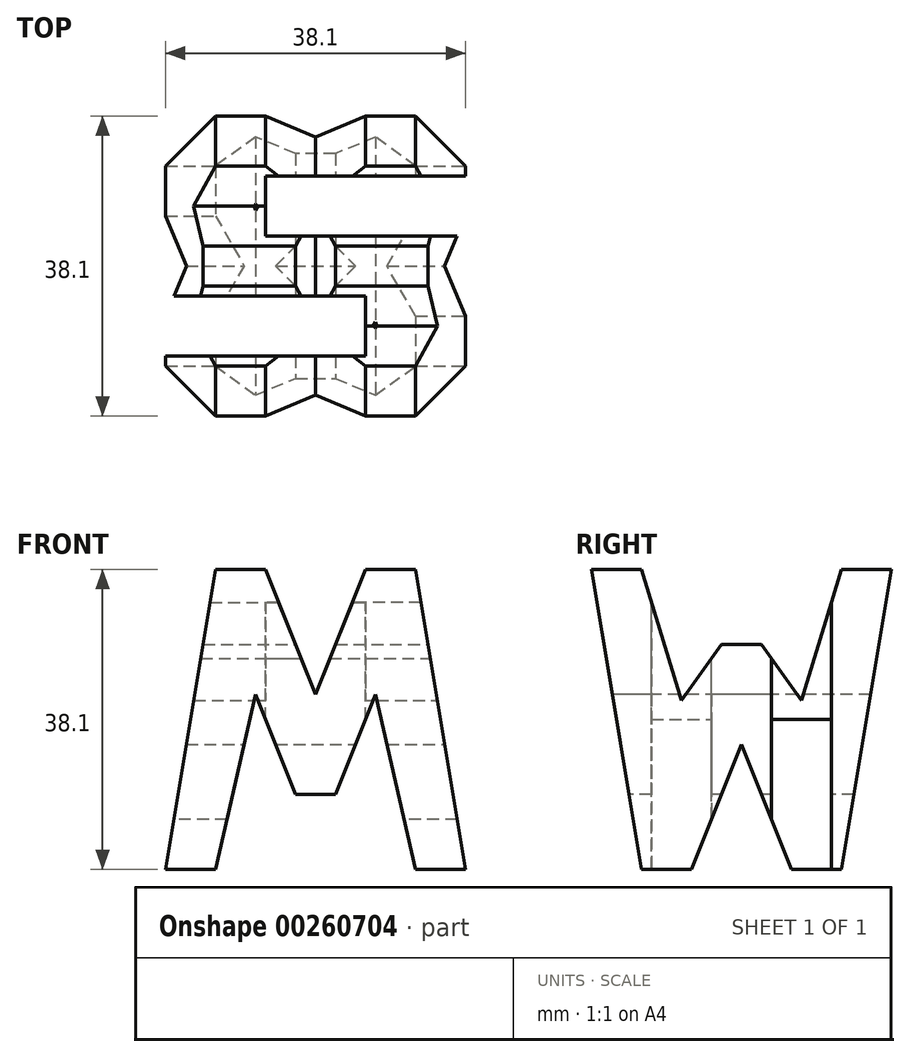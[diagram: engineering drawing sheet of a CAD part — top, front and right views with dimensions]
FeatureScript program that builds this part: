
annotation { "Feature Type Name" : "Feature", "Feature Type Description" : "" }
export const myFeature = defineFeature(function(context is Context, id is Id, definition is map)
    precondition{}
    {
        {
            var Q0;
            Q0=qCreatedBy(makeId("Front.planeOp"),FACE);
            var sketch = newSketch(context, id + "F0", { "sketchPlane" : qUnion([Q0])});
            skLineSegment(sketch, "E0", {"start": v(0, 0) * mm, "end": v(0, 38.1) * mm});
            skLineSegment(sketch, "E1", {"start": v(0, 0) * mm, "end": v(38.1, 0) * mm});
            skLineSegment(sketch, "E2", {"start": v(38.1, 38.1) * mm, "end": v(38.1, 0) * mm});
            skLineSegment(sketch, "E3", {"start": v(38.1, 38.1) * mm, "end": v(0, 38.1) * mm});
            skSolve(sketch);
        }
        {
            var Q0;
            Q0 = qSketchRegion(id + "F0", true);
            extrude(context, id + "F1", {"entities" : qUnion([Q0]), "depth" : 38.1 * mm});
        }
        {
            var Q0;
            Q0=qCreatedBy(makeId("Front.planeOp"),FACE);
            cPlane(context, id + "F2", {"entities" : qUnion([Q0]), "cplaneType" : CPlaneType.OFFSET, "offset" : 38.1 * mm, "width" : 152.4 * mm, "height" : 152.4 * mm});
        }
        {
            var Q0;
            Q0=qCreatedBy(makeId("Right.planeOp"),FACE);
            cPlane(context, id + "F3", {"entities" : qUnion([Q0]), "cplaneType" : CPlaneType.OFFSET, "offset" : 38.1 * mm, "width" : 152.4 * mm, "height" : 152.4 * mm});
        }
        {
            var Q0;
            Q0=qCreatedBy(makeId("Top.planeOp"),FACE);
            cPlane(context, id + "F4", {"entities" : qUnion([Q0]), "cplaneType" : CPlaneType.OFFSET, "offset" : 38.1 * mm, "width" : 152.4 * mm, "height" : 152.4 * mm});
        }
        {
            var Q0;
            Q0=qCreatedBy(id+"F3.planeOp",FACE);
            var sketch = newSketch(context, id + "F5", { "sketchPlane" : qUnion([Q0])});
            skLineSegment(sketch, "E4", {"start": v(0, 0) * mm, "end": v(0, 38.1) * mm});
            skLineSegment(sketch, "E5", {"start": v(0, 38.1) * mm, "end": v(-38.1, 38.1) * mm});
            skLineSegment(sketch, "E6", {"start": v(-38.1, 38.1) * mm, "end": v(-38.1, 0) * mm});
            skLineSegment(sketch, "E7", {"start": v(-38.1, 0) * mm, "end": v(0, 0) * mm});
            skLineSegment(sketch, "E8", {"start": v(-6.35, 0) * mm, "end": v(0, 38.1) * mm});
            skLineSegment(sketch, "E9", {"start": v(-6.35, 38.1) * mm, "end": v(-11.43, 21.48) * mm});
            skLineSegment(sketch, "E10", {"start": v(-11.43, 21.48) * mm, "end": v(-16.51, 28.58) * mm});
            skLineSegment(sketch, "E11", {"start": v(-16.51, 28.58) * mm, "end": v(-21.6, 28.58) * mm});
            skLineSegment(sketch, "E12", {"start": v(-21.6, 28.57) * mm, "end": v(-26.67, 21.48) * mm});
            skPoint(sketch, "E13.end.orphan", {"position": v(-31.75, 38.1) * mm});
            skLineSegment(sketch, "E14", {"start": v(-31.75, 38.1) * mm, "end": v(-26.67, 21.48) * mm});
            skLineSegment(sketch, "E15", {"start": v(-38.1, 38.1) * mm, "end": v(-31.75, 38.1) * mm});
            skLineSegment(sketch, "E16", {"start": v(-38.1, 38.1) * mm, "end": v(-31.75, 0) * mm});
            skLineSegment(sketch, "E17", {"start": v(-31.75, 0) * mm, "end": v(-25.4, 0) * mm});
            skLineSegment(sketch, "E18", {"start": v(-25.4, 0) * mm, "end": v(-19.05, 15.88) * mm});
            skLineSegment(sketch, "E19", {"start": v(-19.05, 15.88) * mm, "end": v(-12.7, 0) * mm});
            skLineSegment(sketch, "E20", {"start": v(-12.7, 0) * mm, "end": v(-6.35, 0) * mm});
            skSolve(sketch);
        }
        {
            var Q0;
            {var subQ2=sQuery(id+"F5.wireOp",EDGE,"E9");Q0=makeQuery(id+"F5.imprint","IMPRINT",FACE,{"disambiguationData":[TD([[makeQuery(id+"F5.imprint","IMPRINT",EDGE,{"derivedFrom":subQ2}),-1.0]])]});}
            var Q1;
            {var subQ0=sQuery(id+"F5.wireOp",EDGE,"E6");Q1=makeQuery(id+"F5.imprint","IMPRINT",FACE,{"disambiguationData":[TD([[makeQuery(id+"F5.imprint","IMPRINT",EDGE,{"derivedFrom":subQ0}),1.0]])]});}
            var Q2;
            {var subQ0=sQuery(id+"F5.wireOp",EDGE,"E18");Q2=makeQuery(id+"F5.imprint","IMPRINT",FACE,{"disambiguationData":[TD([[makeQuery(id+"F5.imprint","IMPRINT",EDGE,{"derivedFrom":subQ0}),-1.0]])]});}
            var Q3;
            {var subQ0=sQuery(id+"F5.wireOp",EDGE,"E4");Q3=makeQuery(id+"F5.imprint","IMPRINT",FACE,{"disambiguationData":[TD([[makeQuery(id+"F5.imprint","IMPRINT",EDGE,{"derivedFrom":subQ0}),1.0]])]});}
            extrude(context, id + "F6", {"entities" : qUnion([Q0, Q1, Q2, Q3]), "operationType" : NewBodyOperationType.REMOVE, "oppositeDirection" : true, "depth" : 38.1 * mm});
        }
        {
            var Q0;
            Q0=qCreatedBy(id+"F2.planeOp",FACE);
            var sketch = newSketch(context, id + "F7", { "sketchPlane" : qUnion([Q0])});
            skLineSegment(sketch, "E21", {"start": v(6.35, 38.1) * mm, "end": v(0, 0) * mm});
            skLineSegment(sketch, "E22", {"start": v(0, 0) * mm, "end": v(6.35, 0) * mm});
            skLineSegment(sketch, "E23", {"start": v(6.35, 0) * mm, "end": v(11.43, 22.22) * mm});
            skLineSegment(sketch, "E24", {"start": v(11.43, 22.22) * mm, "end": v(16.51, 9.52) * mm});
            skLineSegment(sketch, "E25", {"start": v(16.51, 9.52) * mm, "end": v(21.6, 9.52) * mm});
            skLineSegment(sketch, "E26", {"start": v(21.6, 9.52) * mm, "end": v(26.67, 22.22) * mm});
            skLineSegment(sketch, "E27", {"start": v(26.67, 22.22) * mm, "end": v(31.75, 0) * mm});
            skLineSegment(sketch, "E28", {"start": v(31.75, 0) * mm, "end": v(38.1, 0) * mm});
            skLineSegment(sketch, "E29", {"start": v(38.1, 0) * mm, "end": v(31.75, 38.1) * mm});
            skLineSegment(sketch, "E30", {"start": v(31.75, 38.1) * mm, "end": v(25.4, 38.1) * mm});
            skLineSegment(sketch, "E31", {"start": v(25.4, 38.1) * mm, "end": v(19.05, 22.22) * mm});
            skLineSegment(sketch, "E32", {"start": v(19.05, 22.22) * mm, "end": v(12.7, 38.1) * mm});
            skLineSegment(sketch, "E33", {"start": v(12.7, 38.1) * mm, "end": v(6.35, 38.1) * mm});
            skLineSegment(sketch, "E34.bottom", {"start": v(0, 0) * mm, "end": v(38.1, 0) * mm});
            skLineSegment(sketch, "E34.top", {"start": v(0, 38.1) * mm, "end": v(38.1, 38.1) * mm});
            skLineSegment(sketch, "E34.left", {"start": v(0, 0) * mm, "end": v(0, 38.1) * mm});
            skLineSegment(sketch, "E34.right", {"start": v(38.1, 0) * mm, "end": v(38.1, 38.1) * mm});
            skSolve(sketch);
        }
        {
            var Q0;
            {var subQ0=sQuery(id+"F7.wireOp",EDGE,"E23");Q0=makeQuery(id+"F7.imprint","IMPRINT",FACE,{"disambiguationData":[TD([[makeQuery(id+"F7.imprint","IMPRINT",EDGE,{"derivedFrom":subQ0}),-1.0]])]});}
            var Q1;
            {var subQ0=sQuery(id+"F7.wireOp",EDGE,"E21");Q1=makeQuery(id+"F7.imprint","IMPRINT",FACE,{"disambiguationData":[TD([[makeQuery(id+"F7.imprint","IMPRINT",EDGE,{"derivedFrom":subQ0}),-1.0]])]});}
            var Q2;
            {var subQ0=sQuery(id+"F7.wireOp",EDGE,"E31");Q2=makeQuery(id+"F7.imprint","IMPRINT",FACE,{"disambiguationData":[TD([[makeQuery(id+"F7.imprint","IMPRINT",EDGE,{"derivedFrom":subQ0}),-1.0]])]});}
            var Q3;
            {var subQ0=sQuery(id+"F7.wireOp",EDGE,"E29");Q3=makeQuery(id+"F7.imprint","IMPRINT",FACE,{"disambiguationData":[TD([[makeQuery(id+"F7.imprint","IMPRINT",EDGE,{"derivedFrom":subQ0}),-1.0]])]});}
            extrude(context, id + "F8", {"entities" : qUnion([Q0, Q1, Q2, Q3]), "operationType" : NewBodyOperationType.REMOVE, "oppositeDirection" : true, "depth" : 38.1 * mm});
        }
        {
            var Q0;
            Q0=qCreatedBy(id+"F4.planeOp",FACE);
            var sketch = newSketch(context, id + "F9", { "sketchPlane" : qUnion([Q0])});
            skLineSegment(sketch, "E35", {"start": v(0, 0) * mm, "end": v(38.1, 0) * mm});
            skLineSegment(sketch, "E36", {"start": v(38.1, 0) * mm, "end": v(38.1, -38.1) * mm});
            skLineSegment(sketch, "E37", {"start": v(38.1, -38.1) * mm, "end": v(0, -38.1) * mm});
            skLineSegment(sketch, "E38", {"start": v(0, -38.1) * mm, "end": v(0, 0) * mm});
            skLineSegment(sketch, "E39", {"start": v(38.1, -7.62) * mm, "end": v(12.7, -7.62) * mm});
            skLineSegment(sketch, "E40", {"start": v(12.7, -7.62) * mm, "end": v(12.7, -15.24) * mm});
            skLineSegment(sketch, "E41", {"start": v(12.7, -15.24) * mm, "end": v(38.1, -15.24) * mm});
            skLineSegment(sketch, "E42", {"start": v(0, -22.86) * mm, "end": v(25.4, -22.86) * mm});
            skLineSegment(sketch, "E43", {"start": v(25.4, -22.86) * mm, "end": v(25.4, -30.48) * mm});
            skLineSegment(sketch, "E44", {"start": v(25.4, -30.48) * mm, "end": v(0, -30.48) * mm});
            skSolve(sketch);
        }
        {
            var Q0;
            {var subQ0=sQuery(id+"F9.wireOp",EDGE,"E39");Q0=makeQuery(id+"F9.imprint","IMPRINT",FACE,{"disambiguationData":[TD([[makeQuery(id+"F9.imprint","IMPRINT",EDGE,{"derivedFrom":subQ0}),1.0]])]});}
            var Q1;
            {var subQ0=sQuery(id+"F9.wireOp",EDGE,"E42");Q1=makeQuery(id+"F9.imprint","IMPRINT",FACE,{"disambiguationData":[TD([[makeQuery(id+"F9.imprint","IMPRINT",EDGE,{"derivedFrom":subQ0}),-1.0]])]});}
            extrude(context, id + "F10", {"entities" : qUnion([Q0, Q1]), "operationType" : NewBodyOperationType.REMOVE, "oppositeDirection" : true, "depth" : 38.1 * mm});
        }
    });
